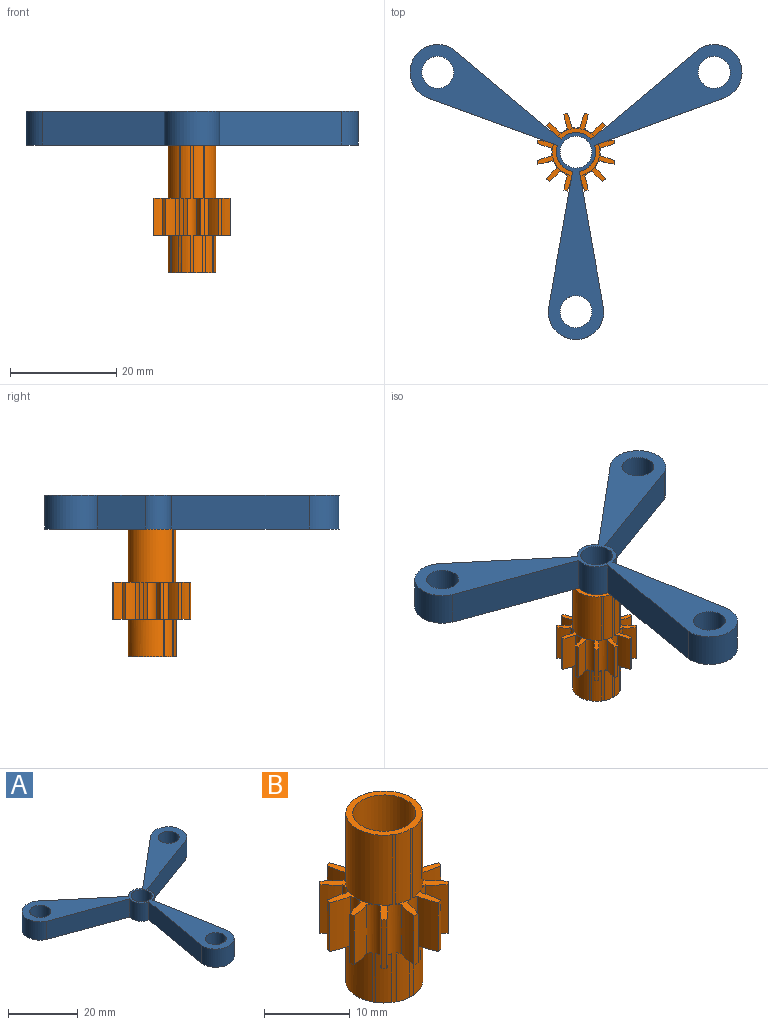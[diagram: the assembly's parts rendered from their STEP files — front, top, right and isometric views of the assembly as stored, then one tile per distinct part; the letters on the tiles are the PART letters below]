
ASSEMBLY  parts=2 mates=1
PART A: 18 faces, bbox 62.4x55.5x6.4 mm
  f0: plane 20.17x16.92mm, normal (-0.64,0.77,0), area 167.2mm2, adj f1,f14,f16,f17
  f1: cylinder r=3.67mm len=6.35mm, axis (0,0,-1), area 40.7mm2, adj f0,f2,f16,f17
  f2: plane 20.17x16.92mm, normal (0.64,0.77,0), area 167.2mm2, adj f1,f3,f16,f17
  f3: cylinder r=5.23mm len=9.97mm, axis (0,0,-1), area 110.1mm2, adj f2,f4,f16,f17
  f4: plane 24.74x9mm, normal (-0.34,-0.94,0), area 167.2mm2, adj f3,f5,f16,f17
  f5: cylinder r=3.67mm len=6.35mm, axis (0,0,-1), area 40.7mm2, adj f4,f6,f16,f17
  f6: plane 25.93x6.35mm, normal (-0.98,0.17,0), area 167.2mm2, adj f5,f7,f16,f17
  f7: cylinder r=5.23mm len=10.46mm, axis (0,0,-1), area 110.1mm2, adj f6,f8,f16,f17
  f8: plane 25.93x6.35mm, normal (0.98,0.17,0), area 167.2mm2, adj f7,f9,f16,f17
  f9: cylinder r=3.67mm len=6.35mm, axis (0,0,-1), area 40.7mm2, adj f8,f10,f16,f17
  f10: plane 24.74x9mm, normal (0.34,-0.94,0), area 167.2mm2, adj f9,f14,f16,f17
  f11: cylinder r=3mm len=6.35mm, axis (0,0,-1), area 119.7mm2, adj f16,f17
  f12: cylinder r=3mm len=6.35mm, axis (0,0,-1), area 119.7mm2, adj f16,f17
  f13: cylinder r=3mm len=6.35mm, axis (0,0,-1), area 119.7mm2, adj f16,f17
  f14: cylinder r=5.23mm len=9.97mm, axis (0,0,-1), area 110.1mm2, adj f0,f10,f16,f17
  f15: cylinder r=3mm len=6.35mm, axis (0,0,-1), area 119.7mm2, adj f16,f17
  f16: plane 62.42x55.46mm, normal (0,0,1), area 527.1mm2, adj f0,f1,f2,f3,f4,f5,f6,f7
  f17: plane 62.42x55.46mm, normal (0,0,-1), area 527.1mm2, adj f0,f1,f2,f3,f4,f5,f6,f7
PART B: 75 faces, bbox 14.6x14.6x24 mm
  f0: plane 3.33x2.06mm, normal (0,0,1), area 2.7mm2, adj f12,f56,f57,f58,f60,f73
  f1: plane 3.33x2.06mm, normal (0,0,1), area 2.7mm2, adj f12,f13,f14,f15,f16,f70
  f2: plane 3.28x3.13mm, normal (0,0,1), area 2.7mm2, adj f16,f17,f18,f19,f20,f71
  f3: plane 14.65x9.58mm, normal (0,0,1), area 22.4mm2, adj f20,f21,f22,f23,f24,f25,f26,f27
  f4: plane 7.35x7.35mm, normal (0,0,1), area 9.2mm2, adj f59,f72
  f5: plane 3.1x3.05mm, normal (0,0,-1), area 2.7mm2, adj f52,f53,f54,f55,f56,f67
  f6: plane 3.27x1.98mm, normal (0,0,-1), area 2.7mm2, adj f12,f56,f57,f58,f60,f66
  f7: plane 3.27x1.98mm, normal (0,0,-1), area 2.7mm2, adj f12,f13,f14,f15,f16,f65
  f8: plane 3.1x3.05mm, normal (0,0,-1), area 2.7mm2, adj f16,f17,f18,f19,f20,f64
  f9: plane 3.32x2.25mm, normal (0,0,-1), area 2.7mm2, adj f48,f49,f50,f51,f52,f63
  f10: plane 14.65x7.33mm, normal (0,0,-1), area 16.7mm2, adj f24,f25,f26,f27,f28,f29,f30,f31
  f11: plane 7.5x7.5mm, normal (0,0,-1), area 11mm2, adj f59,f68
  f12: cylinder r=1.5mm len=24mm, axis (0,0,-1), area 20.2mm2, adj f0,f1,f6,f7,f13,f60,f65,f66
  f13: cylinder r=13mm len=7mm, axis (0,0,-1), area 18.9mm2, adj f1,f7,f12,f14
  f14: cylinder r=7.5mm len=7mm, axis (0,0,-1), area 4.6mm2, adj f1,f7,f13,f15
  f15: cylinder r=13mm len=7mm, axis (0,0,-1), area 18.9mm2, adj f1,f7,f14,f16
  f16: cylinder r=1.5mm len=24mm, axis (0,0,-1), area 19.3mm2, adj f1,f2,f7,f8,f15,f17,f64,f65
  f17: cylinder r=13mm len=7mm, axis (0,0,-1), area 18.9mm2, adj f2,f8,f16,f18
  f18: cylinder r=7.5mm len=7mm, axis (0,0,-1), area 4.6mm2, adj f2,f8,f17,f19
  f19: cylinder r=13mm len=7mm, axis (0,0,-1), area 18.9mm2, adj f2,f8,f18,f20
  f20: cylinder r=1.5mm len=14mm, axis (0,0,-1), area 15mm2, adj f2,f3,f8,f19,f21,f62,f63,f64
  f21: cylinder r=13mm len=7mm, axis (0,0,-1), area 18.9mm2, adj f3,f20,f22,f62
  f22: cylinder r=7.5mm len=7mm, axis (0,0,-1), area 4.6mm2, adj f3,f21,f23,f62
  f23: cylinder r=13mm len=7mm, axis (0,0,-1), area 18.9mm2, adj f3,f22,f24,f62
  f24: cylinder r=1.5mm len=7mm, axis (0,0,-1), area 12.2mm2, adj f3,f10,f23,f25,f62
  f25: cylinder r=13mm len=7mm, axis (0,0,-1), area 18.9mm2, adj f3,f10,f24,f26
  f26: cylinder r=7.5mm len=7mm, axis (0,0,-1), area 4.6mm2, adj f3,f10,f25,f27
  f27: cylinder r=13mm len=7mm, axis (0,0,-1), area 18.9mm2, adj f3,f10,f26,f28
  f28: cylinder r=1.5mm len=7mm, axis (0,0,-1), area 12.2mm2, adj f3,f10,f27,f29
  f29: cylinder r=13mm len=7mm, axis (0,0,-1), area 18.9mm2, adj f3,f10,f28,f30
  f30: cylinder r=7.5mm len=7mm, axis (0,0,-1), area 4.6mm2, adj f3,f10,f29,f31
  f31: cylinder r=13mm len=7mm, axis (0,0,-1), area 18.9mm2, adj f3,f10,f30,f32
  f32: cylinder r=1.5mm len=7mm, axis (0,0,-1), area 12.2mm2, adj f3,f10,f31,f33
  f33: cylinder r=13mm len=7mm, axis (0,0,-1), area 18.9mm2, adj f3,f10,f32,f34
  f34: cylinder r=7.5mm len=7mm, axis (0,0,-1), area 4.6mm2, adj f3,f10,f33,f35
  f35: cylinder r=13mm len=7mm, axis (0,0,-1), area 18.9mm2, adj f3,f10,f34,f36
  f36: cylinder r=1.5mm len=7mm, axis (0,0,-1), area 12.2mm2, adj f3,f10,f35,f37
  f37: cylinder r=13mm len=7mm, axis (0,0,-1), area 18.9mm2, adj f3,f10,f36,f38
  f38: cylinder r=7.5mm len=7mm, axis (0,0,-1), area 4.6mm2, adj f3,f10,f37,f39
  f39: cylinder r=13mm len=7mm, axis (0,0,-1), area 18.9mm2, adj f3,f10,f38,f40
  f40: cylinder r=1.5mm len=7mm, axis (0,0,-1), area 12.2mm2, adj f3,f10,f39,f41
  f41: cylinder r=13mm len=7mm, axis (0,0,-1), area 18.9mm2, adj f3,f10,f40,f42
  f42: cylinder r=7.5mm len=7mm, axis (0,0,-1), area 4.6mm2, adj f3,f10,f41,f43
  f43: cylinder r=13mm len=7mm, axis (0,0,-1), area 18.9mm2, adj f3,f10,f42,f44
  f44: cylinder r=1.5mm len=7mm, axis (0,0,-1), area 12.2mm2, adj f3,f10,f43,f45
  f45: cylinder r=13mm len=7mm, axis (0,0,-1), area 18.9mm2, adj f3,f10,f44,f46
  f46: cylinder r=7.5mm len=7mm, axis (0,0,-1), area 4.6mm2, adj f3,f10,f45,f47
  f47: cylinder r=13mm len=7mm, axis (0,0,-1), area 18.9mm2, adj f3,f10,f46,f48
  f48: cylinder r=1.5mm len=7mm, axis (0,0,-1), area 12.2mm2, adj f3,f9,f10,f47,f49
  f49: cylinder r=13mm len=7mm, axis (0,0,-1), area 18.9mm2, adj f3,f9,f48,f50
  f50: cylinder r=7.5mm len=7mm, axis (0,0,-1), area 4.6mm2, adj f3,f9,f49,f51
  f51: cylinder r=13mm len=7mm, axis (0,0,-1), area 18.9mm2, adj f3,f9,f50,f52
  f52: cylinder r=1.5mm len=14mm, axis (0,0,-1), area 15mm2, adj f3,f5,f9,f51,f53,f61,f63,f67
  f53: cylinder r=13mm len=7mm, axis (0,0,-1), area 18.9mm2, adj f5,f52,f54,f61
  f54: cylinder r=7.5mm len=7mm, axis (0,0,-1), area 4.6mm2, adj f5,f53,f55,f61
  f55: cylinder r=13mm len=7mm, axis (0,0,-1), area 18.9mm2, adj f5,f54,f56,f61
  f56: cylinder r=1.5mm len=24mm, axis (0,0,-1), area 19.3mm2, adj f0,f5,f6,f55,f57,f61,f66,f67
  f57: cylinder r=13mm len=7mm, axis (0,0,-1), area 18.9mm2, adj f0,f6,f56,f58
  f58: cylinder r=7.5mm len=7mm, axis (0,0,-1), area 4.6mm2, adj f0,f6,f57,f60
  f59: cylinder r=3.25mm len=7mm, axis (0,0,-1), area 142.9mm2, adj f4,f11
  f60: cylinder r=13mm len=7mm, axis (0,0,-1), area 18.9mm2, adj f0,f6,f12,f58
  f61: plane 3.28x3.13mm, normal (0,0,1), area 2.7mm2, adj f52,f53,f54,f55,f56,f71
  f62: plane 3.32x2.25mm, normal (0,0,-1), area 2.7mm2, adj f20,f21,f22,f23,f24,f63
  f63: cylinder r=4.5mm len=9mm, axis (0,0,1), area 128.8mm2, adj f9,f10,f20,f52,f62,f69
  f64: cylinder r=4.5mm len=7mm, axis (0,0,1), area 13.3mm2, adj f8,f16,f20,f69
  f65: cylinder r=4.5mm len=7mm, axis (0,0,1), area 12.8mm2, adj f7,f12,f16,f69
  f66: cylinder r=4.5mm len=7mm, axis (0,0,1), area 12.8mm2, adj f6,f12,f56,f69
  f67: cylinder r=4.5mm len=7mm, axis (0,0,1), area 13.3mm2, adj f5,f52,f56,f69
  f68: cylinder r=3.75mm len=7.5mm, axis (0,0,1), area 164.9mm2, adj f11,f69
  f69: plane 9x8.99mm, normal (0,0,-1), area 19.4mm2, adj f12,f16,f20,f52,f56,f63,f64,f65
  f70: cylinder r=4.48mm len=10mm, axis (0,0,-1), area 19.9mm2, adj f1,f12,f16,f74
  f71: cylinder r=4.48mm len=10mm, axis (0,0,-1), area 231mm2, adj f2,f3,f16,f56,f61,f74
  f72: cylinder r=3.67mm len=10mm, axis (0,0,-1), area 230.9mm2, adj f4,f74
  f73: cylinder r=4.48mm len=10mm, axis (0,0,-1), area 19.9mm2, adj f0,f12,f56,f74
  f74: plane 8.96x8.96mm, normal (0,0,1), area 20.7mm2, adj f12,f16,f56,f70,f71,f72,f73
PLACE A t=(21.82,13.35,18.29)mm
PLACE B t=(21.82,13.35,1.29)mm
MATE fastened B.f70 <-> A.f15  axis (0,0,-1) through (21.82,13.35,18.29)mm
